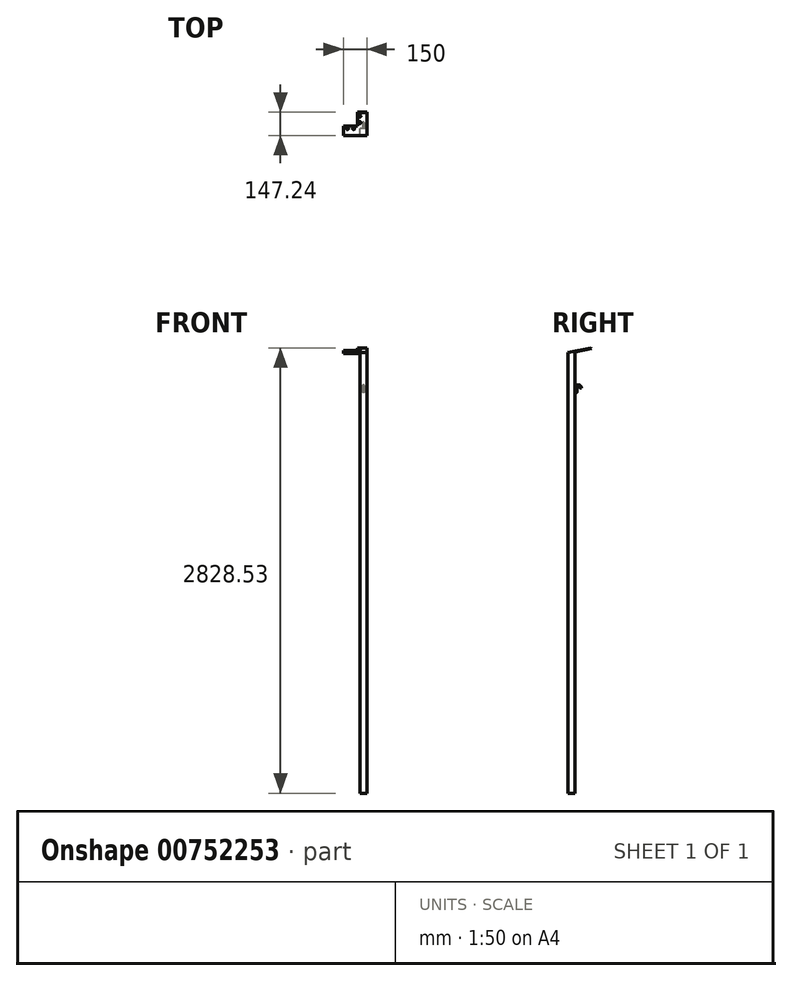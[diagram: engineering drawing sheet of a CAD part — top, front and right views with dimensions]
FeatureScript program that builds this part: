
annotation { "Feature Type Name" : "Feature", "Feature Type Description" : "" }
export const myFeature = defineFeature(function(context is Context, id is Id, definition is map)
    precondition{}
    {
        {
            var Q0;
            Q0=qCreatedBy(makeId("Top.planeOp"),FACE);
            var sketch = newSketch(context, id + "F0", { "sketchPlane" : qUnion([Q0])});
            skLineSegment(sketch, "E0.bottom", {"start": v(22.5, -22.5) * mm, "end": v(-22.5, -22.5) * mm});
            skLineSegment(sketch, "E0.top", {"start": v(22.5, 22.5) * mm, "end": v(-22.5, 22.5) * mm});
            skLineSegment(sketch, "E0.left", {"start": v(22.5, -22.5) * mm, "end": v(22.5, 22.5) * mm});
            skLineSegment(sketch, "E0.right", {"start": v(-22.5, -22.5) * mm, "end": v(-22.5, 22.5) * mm});
            skPoint(sketch, "E0.middle", {"position": v(0, 0) * mm});
            skSolve(sketch);
        }
        {
            var Q0;
            Q0=qSketchRegion(id+"F0",true);
            extrude(context, id + "F1", {"entities" : qUnion([Q0]), "depth" : 2795 * mm, "offsetDistance" : 25 * mm});
        }
        {
            var Q0;
            Q0=makeQuery(id+"F1.opExtrude","CAP_EDGE",EDGE,{"disambiguationData":[OSD([sQuery(id+"F0.wireOp",EDGE,"E0.bottom")])],"isStart":false});
            cPlane(context, id + "F2", {"entities" : qUnion([Q0]), "cplaneType" : CPlaneType.LINE_ANGLE, "offset" : 25 * mm, "angle" : 79 * degree, "width" : 150 * mm, "height" : 150 * mm});
        }
        {
            var Q0;
            Q0=qCreatedBy(id+"F2.planeOp",FACE);
            var sketch = newSketch(context, id + "F3", { "sketchPlane" : qUnion([Q0])});
            skLineSegment(sketch, "E1.bottom", {"start": v(-37.5, 511.22) * mm, "end": v(22.5, 511.22) * mm});
            skLineSegment(sketch, "E1.top", {"start": v(-37.5, 661.22) * mm, "end": v(22.5, 661.22) * mm});
            skLineSegment(sketch, "E1.left", {"start": v(-37.5, 511.22) * mm, "end": v(-37.5, 661.22) * mm});
            skLineSegment(sketch, "E1.right", {"start": v(22.5, 511.22) * mm, "end": v(22.5, 661.22) * mm});
            skLineSegment(sketch, "E2.left", {"start": v(7.5, 511.22) * mm, "end": v(7.5, 571.22) * mm});
            skLineSegment(sketch, "E3.bottom", {"start": v(22.5, 571.22) * mm, "end": v(-127.5, 571.22) * mm});
            skLineSegment(sketch, "E3.top", {"start": v(22.5, 511.22) * mm, "end": v(-127.5, 511.22) * mm});
            skLineSegment(sketch, "E3.left", {"start": v(22.5, 571.22) * mm, "end": v(22.5, 511.22) * mm});
            skLineSegment(sketch, "E3.right", {"start": v(-127.5, 571.22) * mm, "end": v(-127.5, 511.22) * mm});
            skLineSegment(sketch, "E4", {"start": v(7.5, 571.22) * mm, "end": v(22.5, 571.22) * mm});
            skSolve(sketch);
        }
        {
            var Q0;
            Q0=qSketchRegion(id+"F3",true);
            extrude(context, id + "F4", {"entities" : qUnion([Q0]), "depth" : 5 * mm, "offsetDistance" : 25 * mm});
        }
        {
            var Q0;
            Q0=makeQuery(id+"F1.opExtrude","SWEPT_FACE",FACE,{"disambiguationData":[OSD([sQuery(id+"F0.wireOp",EDGE,"E0.left")])]});
            var sketch = newSketch(context, id + "F5", { "sketchPlane" : qUnion([Q0])});
            skLineSegment(sketch, "E5", {"start": v(22.5, 2795) * mm, "end": v(22.5, 2803.75) * mm});
            skLineSegment(sketch, "E6", {"start": v(22.5, 2803.75) * mm, "end": v(-22.5, 2795) * mm});
            skLineSegment(sketch, "E7", {"start": v(-22.5, 2795) * mm, "end": v(22.5, 2795) * mm});
            skSolve(sketch);
        }
        {
            var Q0;
            Q0=qSketchRegion(id+"F5",true);
            extrude(context, id + "F6", {"entities" : qUnion([Q0]), "oppositeDirection" : true, "depth" : 45 * mm, "offsetDistance" : 25 * mm});
        }
        {
            var Q0;
            Q0=makeQuery(id+"F1.opExtrude","SWEPT_BODY",BODY,{"disambiguationData":[OSD([sQuery(id+"F0.wireOp",EDGE,"E0.bottom"),sQuery(id+"F0.wireOp",EDGE,"E0.top"),sQuery(id+"F0.wireOp",EDGE,"E0.left"),sQuery(id+"F0.wireOp",EDGE,"E0.right")])]});
            var Q1;
            Q1=makeQuery(id+"F6.opExtrude","SWEPT_BODY",BODY,{"disambiguationData":[OSD([sQuery(id+"F5.wireOp",EDGE,"E5"),sQuery(id+"F5.wireOp",EDGE,"E6"),sQuery(id+"F5.wireOp",EDGE,"E7")])]});
            var Q2;
            Q2=makeQuery(id+"F4.opExtrude","SWEPT_BODY",BODY,{"disambiguationData":[OSD([sQuery(id+"F3.wireOp",EDGE,"E1.bottom"),sQuery(id+"F3.wireOp",EDGE,"E1.top"),sQuery(id+"F3.wireOp",EDGE,"E1.left"),sQuery(id+"F3.wireOp",EDGE,"E1.right"),sQuery(id+"F3.wireOp",EDGE,"E2.bottom"),sQuery(id+"F3.wireOp",EDGE,"E2.top"),sQuery(id+"F3.wireOp",EDGE,"E2.right")])]});
            booleanBodies(context, id + "F7", {"operationType" : BooleanOperationType.UNION, "tools" : qUnion([Q0, Q1, Q2])});
        }
        {
            var Q0;
            Q0=makeQuery(id+"F7.opBoolean","MERGE",FACE,{"derivedFrom":[makeQuery(id+"F1.opExtrude","SWEPT_FACE",FACE,{"disambiguationData":[OSD([sQuery(id+"F0.wireOp",EDGE,"E0.right")])]}),makeQuery(id+"F4.opExtrude","SWEPT_FACE",FACE,{"disambiguationData":[OSD([sQuery(id+"F3.wireOp",EDGE,"E1.left")])]}),makeQuery(id+"F6.opExtrude","CAP_FACE",FACE,{"disambiguationData":[OSD([sQuery(id+"F5.wireOp",EDGE,"E5"),sQuery(id+"F5.wireOp",EDGE,"E6"),sQuery(id+"F5.wireOp",EDGE,"E7")])],"isStart":false})]});
            var sketch = newSketch(context, id + "F8", { "sketchPlane" : qUnion([Q0])});
            skLineSegment(sketch, "E8", {"start": v(9.37, 2795) * mm, "end": v(22.5, 2795) * mm});
            skLineSegment(sketch, "E9.bottom", {"start": v(22.5, 2795) * mm, "end": v(25.28, 2795) * mm});
            skLineSegment(sketch, "E9.top", {"start": v(22.5, 2800.7) * mm, "end": v(25.28, 2800.7) * mm});
            skLineSegment(sketch, "E9.left", {"start": v(22.5, 2795) * mm, "end": v(22.5, 2800.7) * mm});
            skLineSegment(sketch, "E9.right", {"start": v(25.28, 2795) * mm, "end": v(25.28, 2800.7) * mm});
            skSolve(sketch);
        }
        {
            var Q0;
            Q0=qSketchRegion(id+"F8",true);
            var Q1;
            Q1=makeQuery(id+"F4.opExtrude","SWEPT_FACE",FACE,{"disambiguationData":[OSD([sQuery(id+"F3.wireOp",EDGE,"E2.right")])]});
            var Q2;
            Q2=makeQuery(id+"F4.opExtrude","SWEPT_FACE",FACE,{"disambiguationData":[OSD([sQuery(id+"F3.wireOp",EDGE,"E3.right")])]});
            extrude(context, id + "F9", {"entities" : qUnion([Q0]), "operationType" : NewBodyOperationType.REMOVE, "oppositeDirection" : true, "depth" : 156.8 * mm, "endBoundEntityFace" : qUnion([Q1]), "offsetDistance" : 25 * mm, "hasSecondDirection" : true, "secondDirectionBound" : SecondDirectionBoundingType.UP_TO_SURFACE, "secondDirectionOppositeDirection" : false, "secondDirectionDepth" : 25 * mm, "secondDirectionBoundEntityFace" : qUnion([Q2])});
        }
        {
            var Q0;
            Q0=qCreatedBy(makeId("Top.planeOp"),FACE);
            cPlane(context, id + "F10", {"entities" : qUnion([Q0]), "cplaneType" : CPlaneType.OFFSET, "offset" : 2545 * mm, "width" : 150 * mm, "height" : 150 * mm});
        }
        {
            var Q0;
            Q0=qCreatedBy(makeId("Right.planeOp"),FACE);
            var sketch = newSketch(context, id + "F11", { "sketchPlane" : qUnion([Q0])});
            skLineSegment(sketch, "E10", {"start": v(27.5, 2545) * mm, "end": v(27.5, 2575) * mm});
            skLineSegment(sketch, "E11", {"start": v(27.5, 2575) * mm, "end": v(57.5, 2575) * mm});
            skArc(sketch, "E12", {"start": v(57.5, 2575) * mm, "mid": v(42.5, 2590) * mm, "end": v(27.5, 2575) * mm});
            skLineSegment(sketch, "E13", {"start": v(27.5, 2545) * mm, "end": v(22.5, 2545) * mm});
            skSolve(sketch);
        }
        {
            var Q0;
            Q0=qCreatedBy(id+"F10.planeOp",FACE);
            var sketch = newSketch(context, id + "F12", { "sketchPlane" : qUnion([Q0])});
            skCircle(sketch, "E14", {"center": v(0, 27.5) * mm, "radius": 5 * mm});
            skLineSegment(sketch, "E15", {"start": v(0, 27.5) * mm, "end": v(0, 22.5) * mm});
            skLineSegment(sketch, "E16", {"start": v(0, 22.5) * mm, "end": v(-5, 22.5) * mm});
            skLineSegment(sketch, "E17", {"start": v(0, 27.5) * mm, "end": v(-5, 27.5) * mm});
            skLineSegment(sketch, "E18", {"start": v(-5, 27.5) * mm, "end": v(-5, 22.5) * mm});
            skLineSegment(sketch, "E19", {"start": v(0, 27.5) * mm, "end": v(5, 27.5) * mm});
            skLineSegment(sketch, "E20", {"start": v(5, 27.5) * mm, "end": v(5, 22.5) * mm});
            skLineSegment(sketch, "E21", {"start": v(0, 22.5) * mm, "end": v(5, 22.5) * mm});
            skSolve(sketch);
        }
        {
            var Q0;
            Q0=makeQuery(id+"F4.opExtrude","CAP_FACE",FACE,{"disambiguationData":[OSD([sQuery(id+"F3.wireOp",EDGE,"E1.top"),sQuery(id+"F3.wireOp",EDGE,"E1.left"),sQuery(id+"F3.wireOp",EDGE,"E1.right"),sQuery(id+"F3.wireOp",EDGE,"E3.bottom"),sQuery(id+"F3.wireOp",EDGE,"E3.top"),sQuery(id+"F3.wireOp",EDGE,"E3.left"),sQuery(id+"F3.wireOp",EDGE,"E3.right")])],"isStart":false});
            var sketch = newSketch(context, id + "F13", { "sketchPlane" : qUnion([Q0])});
            skLineSegment(sketch, "E22", {"start": v(22.5, 511.22) * mm, "end": v(-22.5, 511.22) * mm});
            skLineSegment(sketch, "E23", {"start": v(-22.5, 511.22) * mm, "end": v(-22.5, 596.22) * mm});
            skLineSegment(sketch, "E24", {"start": v(-22.5, 512.2) * mm, "end": v(-62.5, 512.2) * mm});
            skLineSegment(sketch, "E25", {"start": v(-62.5, 512.2) * mm, "end": v(-102.5, 512.2) * mm});
            skLineSegment(sketch, "E26", {"start": v(-62.5, 512.2) * mm, "end": v(-62.5, 556.22) * mm});
            skCircle(sketch, "E27", {"center": v(-102.5, 556.22) * mm, "radius": 6 * mm});
            skCircle(sketch, "E28", {"center": v(-62.5, 556.22) * mm, "radius": 6 * mm});
            skCircle(sketch, "E29", {"center": v(-22.5, 596.22) * mm, "radius": 6 * mm});
            skCircle(sketch, "E30", {"center": v(-22.5, 636.22) * mm, "radius": 6 * mm});
            skLineSegment(sketch, "E31", {"start": v(22.5, 661.22) * mm, "end": v(22.5, 511.22) * mm});
            skLineSegment(sketch, "E32", {"start": v(-102.5, 556.22) * mm, "end": v(-127.5, 556.22) * mm});
            skLineSegment(sketch, "E33", {"start": v(-22.5, 636.22) * mm, "end": v(-22.5, 661.22) * mm});
            skSolve(sketch);
        }
        {
            var Q0;
            Q0=makeQuery(id+"F13.imprint","IMPRINT",FACE,{"disambiguationData":[TD([[makeQuery(id+"F13.imprint","IMPRINT",EDGE,{"derivedFrom":sQuery(id+"F13.wireOp",EDGE,"E28")}),1.0]])]});
            var Q1;
            Q1=makeQuery(id+"F13.imprint","IMPRINT",FACE,{"disambiguationData":[TD([[makeQuery(id+"F13.imprint","IMPRINT",EDGE,{"derivedFrom":sQuery(id+"F13.wireOp",EDGE,"E27")}),1.0]])]});
            var Q2;
            Q2=makeQuery(id+"F13.imprint","IMPRINT",FACE,{"disambiguationData":[TD([[makeQuery(id+"F13.imprint","IMPRINT",EDGE,{"derivedFrom":sQuery(id+"F13.wireOp",EDGE,"E29")}),1.0]])]});
            var Q3;
            Q3=makeQuery(id+"F13.imprint","IMPRINT",FACE,{"disambiguationData":[TD([[makeQuery(id+"F13.imprint","IMPRINT",EDGE,{"derivedFrom":sQuery(id+"F13.wireOp",EDGE,"E30")}),1.0]])]});
            var Q4;
            Q4=makeQuery(id+"F4.opExtrude","CAP_FACE",FACE,{"disambiguationData":[OSD([sQuery(id+"F3.wireOp",EDGE,"E1.top"),sQuery(id+"F3.wireOp",EDGE,"E1.left"),sQuery(id+"F3.wireOp",EDGE,"E1.right"),sQuery(id+"F3.wireOp",EDGE,"E3.bottom"),sQuery(id+"F3.wireOp",EDGE,"E3.top"),sQuery(id+"F3.wireOp",EDGE,"E3.left"),sQuery(id+"F3.wireOp",EDGE,"E3.right")])],"isStart":true});
            extrude(context, id + "F14", {"entities" : qUnion([Q0, Q1, Q2, Q3]), "operationType" : NewBodyOperationType.REMOVE, "endBound" : BoundingType.UP_TO_SURFACE, "oppositeDirection" : true, "depth" : 25 * mm, "endBoundEntityFace" : qUnion([Q4]), "offsetDistance" : 25 * mm});
        }
        {
            var Q0;
            Q0 = qSketchRegion(id + "F12", true);
            extrude(context, id + "F15", {"entities" : qUnion([Q0]), "operationType" : NewBodyOperationType.ADD, "depth" : 30 * mm, "offsetDistance" : 25 * mm});
        }
        {
            var Q0;
            Q0=makeQuery(id+"F15.opExtrude","CAP_FACE",FACE,{"disambiguationData":[OSD([sQuery(id+"F12.wireOp",EDGE,"E14"),sQuery(id+"F12.wireOp",EDGE,"E16"),sQuery(id+"F12.wireOp",EDGE,"E18"),sQuery(id+"F12.wireOp",EDGE,"E20"),sQuery(id+"F12.wireOp",EDGE,"E21")])],"isStart":false});
            var sketch = newSketch(context, id + "F16", { "sketchPlane" : qUnion([Q0])});
            skArc(sketch, "E34.0", {"start": v(5, 27.5) * mm, "mid": v(0, 32.5) * mm, "end": v(-5, 27.5) * mm});
            skLineSegment(sketch, "E35", {"start": v(5, 27.5) * mm, "end": v(0, 27.5) * mm});
            skArc(sketch, "E36.MirrorCS", {"start": v(5, 27.5) * mm, "mid": v(0, 22.5) * mm, "end": v(-5, 27.5) * mm});
            skSolve(sketch);
        }
        {
            var Q0;
            {var subQ0=sQuery(id+"F16.wireOp",EDGE,"E34.0");Q0=makeQuery(id+"F16.imprint","IMPRINT",FACE,{"disambiguationData":[TD([[makeQuery(id+"F16.imprint","IMPRINT",EDGE,{"derivedFrom":subQ0}),1.0]])]});}
            var Q1;
            Q1=sQuery(id+"F11.wireOp",EDGE,"E12");
            sweep(context, id + "F17", {"operationType" : NewBodyOperationType.ADD, "profiles" : qUnion([Q0]), "path" : qUnion([Q1])});
        }
    });
